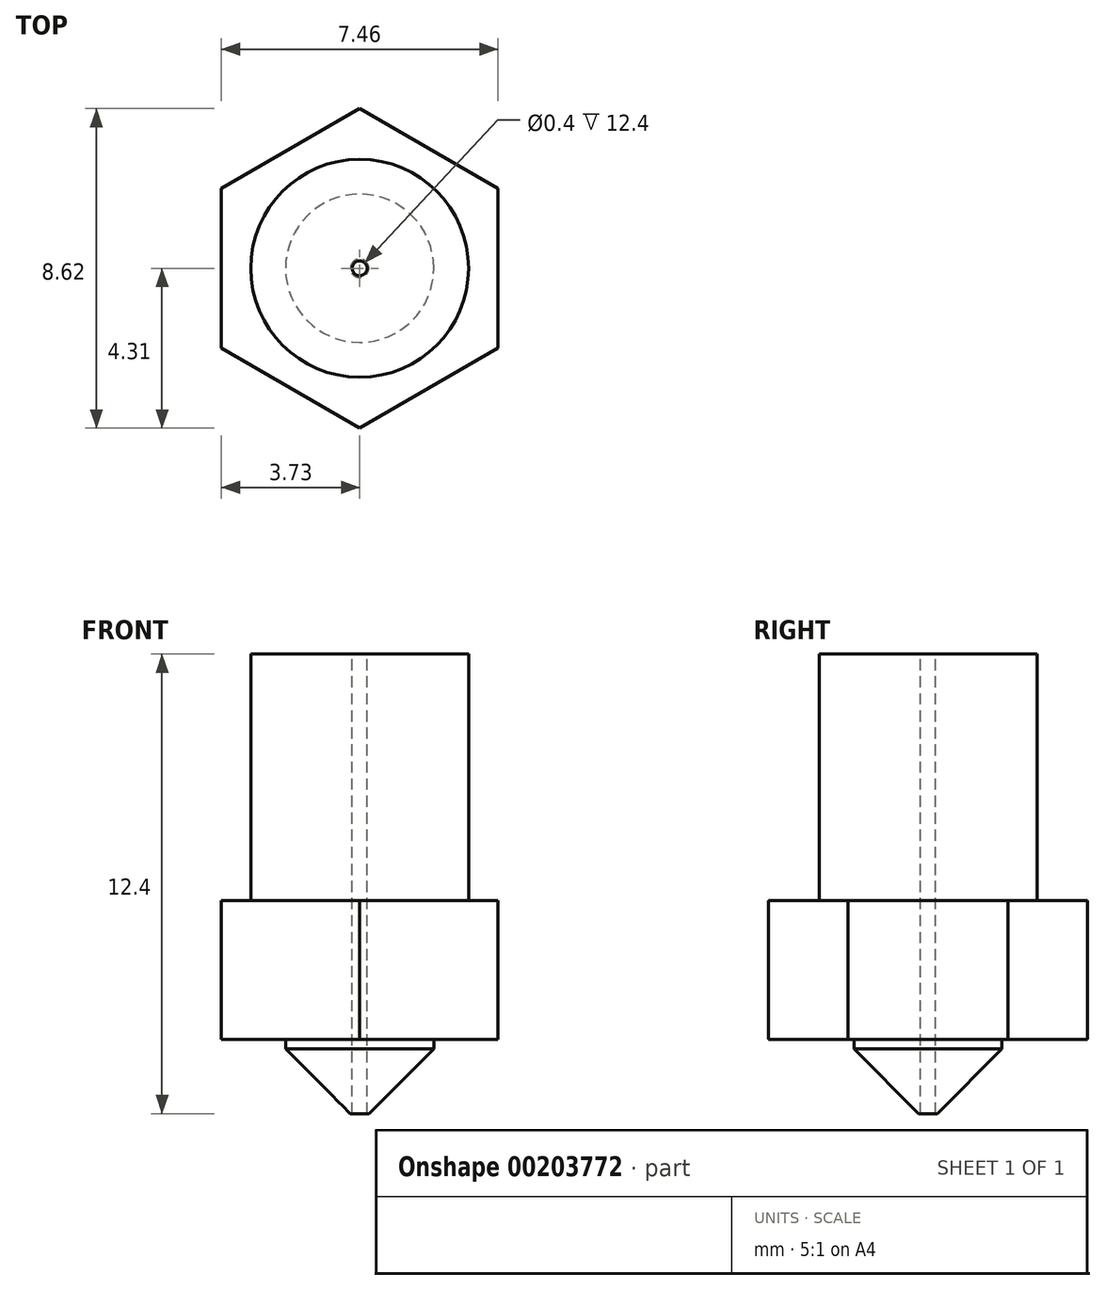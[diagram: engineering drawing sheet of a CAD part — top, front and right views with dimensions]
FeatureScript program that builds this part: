
annotation { "Feature Type Name" : "Feature", "Feature Type Description" : "" }
export const myFeature = defineFeature(function(context is Context, id is Id, definition is map)
    precondition{}
    {
        {
            var Q0;
            Q0=qCreatedBy(makeId("Top.planeOp"),FACE);
            var sketch = newSketch(context, id + "F0", { "sketchPlane" : qUnion([Q0])});
            skCircle(sketch, "E0.cCircle", {"center": v(0, 0) * mm, "radius": 3.73 * mm, "construction": true});
            skLineSegment(sketch, "E0.0", {"start": v(3.73, 2.15) * mm, "end": v(3.73, -2.15) * mm});
            skLineSegment(sketch, "E0.1", {"start": v(3.73, -2.15) * mm, "end": v(0, -4.3) * mm});
            skLineSegment(sketch, "E0.2", {"start": v(0, -4.3) * mm, "end": v(-3.73, -2.15) * mm});
            skLineSegment(sketch, "E0.3", {"start": v(-3.73, -2.15) * mm, "end": v(-3.73, 2.15) * mm});
            skLineSegment(sketch, "E0.4", {"start": v(-3.73, 2.15) * mm, "end": v(0, 4.3) * mm});
            skLineSegment(sketch, "E0.5", {"start": v(0, 4.3) * mm, "end": v(3.73, 2.15) * mm});
            skPoint(sketch, "E0.0.midPoint", {"position": v(3.73, 0) * mm});
            skSolve(sketch);
        }
        {
            var Q0;
            Q0=makeQuery(id+"F0.imprint","IMPRINT",FACE,{"disambiguationData":[TD([[makeQuery(id+"F0.imprint","IMPRINT",EDGE,{"derivedFrom":sQuery(id+"F0.wireOp",EDGE,"E0.0")}),-1.0]])]});
            extrude(context, id + "F1", {"entities" : qUnion([Q0]), "oppositeDirection" : true, "depth" : 3.75 * mm});
        }
        {
            var Q0;
            Q0=makeQuery(id+"F1.opExtrude","CAP_FACE",FACE,{"disambiguationData":[OSD([sQuery(id+"F0.wireOp",EDGE,"E0.0"),sQuery(id+"F0.wireOp",EDGE,"E0.1"),sQuery(id+"F0.wireOp",EDGE,"E0.2"),sQuery(id+"F0.wireOp",EDGE,"E0.3"),sQuery(id+"F0.wireOp",EDGE,"E0.4"),sQuery(id+"F0.wireOp",EDGE,"E0.5")])],"isStart":true});
            var sketch = newSketch(context, id + "F2", { "sketchPlane" : qUnion([Q0])});
            skCircle(sketch, "E1", {"center": v(0, 0) * mm, "radius": 2.94 * mm});
            skSolve(sketch);
        }
        {
            var Q0;
            Q0=makeQuery(id+"F2.imprint","IMPRINT",FACE,{"disambiguationData":[TD([[makeQuery(id+"F2.imprint","IMPRINT",EDGE,{"derivedFrom":sQuery(id+"F2.wireOp",EDGE,"E1")}),1.0]])]});
            extrude(context, id + "F3", {"entities" : qUnion([Q0]), "operationType" : NewBodyOperationType.ADD, "depth" : 6.65 * mm});
        }
        {
            var Q0;
            Q0=makeQuery(id+"F1.opExtrude","CAP_FACE",FACE,{"disambiguationData":[OSD([sQuery(id+"F0.wireOp",EDGE,"E0.0"),sQuery(id+"F0.wireOp",EDGE,"E0.1"),sQuery(id+"F0.wireOp",EDGE,"E0.2"),sQuery(id+"F0.wireOp",EDGE,"E0.3"),sQuery(id+"F0.wireOp",EDGE,"E0.4"),sQuery(id+"F0.wireOp",EDGE,"E0.5")])],"isStart":false});
            var sketch = newSketch(context, id + "F4", { "sketchPlane" : qUnion([Q0])});
            skCircle(sketch, "E2", {"center": v(0, 0) * mm, "radius": 2 * mm});
            skSolve(sketch);
        }
        {
            var Q0;
            Q0=makeQuery(id+"F4.imprint","IMPRINT",FACE,{"disambiguationData":[TD([[makeQuery(id+"F4.imprint","IMPRINT",EDGE,{"derivedFrom":sQuery(id+"F4.wireOp",EDGE,"E2")}),1.0]])]});
            extrude(context, id + "F5", {"entities" : qUnion([Q0]), "operationType" : NewBodyOperationType.ADD, "depth" : 2 * mm});
        }
        {
            var Q0;
            Q0=makeQuery(id+"F5.opExtrude","CAP_EDGE",EDGE,{"disambiguationData":[OSD([sQuery(id+"F4.wireOp",EDGE,"E2")])],"isStart":false});
            chamfer(context, id + "F6", {"entities" : qUnion([Q0]), "width" : 1.75 * mm, "tangentPropagation" : true});
        }
        {
            var Q0;
            Q0=makeQuery(id+"F3.opExtrude","CAP_FACE",FACE,{"disambiguationData":[OSD([sQuery(id+"F2.wireOp",EDGE,"E1")])],"isStart":false});
            var sketch = newSketch(context, id + "F7", { "sketchPlane" : qUnion([Q0])});
            skCircle(sketch, "E3", {"center": v(0, 0) * mm, "radius": 0.2 * mm});
            skSolve(sketch);
        }
        {
            var Q0;
            Q0=makeQuery(id+"F7.imprint","IMPRINT",FACE,{"disambiguationData":[TD([[makeQuery(id+"F7.imprint","IMPRINT",EDGE,{"derivedFrom":sQuery(id+"F7.wireOp",EDGE,"E3")}),1.0]])]});
            extrude(context, id + "F8", {"entities" : qUnion([Q0]), "operationType" : NewBodyOperationType.REMOVE, "endBound" : BoundingType.UP_TO_NEXT, "oppositeDirection" : true, "depth" : 25 * mm});
        }
    });
